AUTODESK INVENTOR PART (.ipt)
format: ipt  version: 2019 (Build 230136000, 136)  size: 151,552 bytes
history: native  units: mm
features: extrude x3, sketch x3, other x1, fillet x1, projected_geometry x1
ambient origin geometry x8: Origin, YZ Plane, XZ Plane, XY Plane, X Axis, Y Axis, Z Axis, Center Point
bodies: Body1 (feature_tree)
feature tree (9):
  other  "Твердое тело1"
  extrude  "Выдавливание1"  Depth=2.5mm
  extrude  "Выдавливание2"  Depth=3.0mm TaperAngle=0.0deg
  fillet  "Сопряжение1"  Radius=1.0mm
  extrude  "Выдавливание3"  Depth=2.0mm
  sketch  "Эскиз1"
  sketch  "Эскиз2"
  projected_geometry  "Спроецированная петля1"
  sketch  "Эскиз3"
